FCSTD DOCUMENT  (FreeCAD 0.18.1R)
Label: LED_hole_test
License: All rights reserved
LicenseURL: http://en.wikipedia.org/wiki/All_rights_reserved
objects: Sketcher::SketchObject×1, PartDesign::Body×1
note: 2 computed .brp shape members not serialized (recipe doc carries the construction recipe); baked Part::Feature solids carry a one-line shape summary decoded from their .brp

FEATURE [Sketcher::SketchObject] Sketch
  MapMode = 5
  Support = -> [XY_Plane]
  sketch-geometry (28):
    g0: LineSegment StartX=0 StartY=0 StartZ=0 EndX=25 EndY=0 EndZ=0
    g1: LineSegment StartX=25 StartY=0 StartZ=0 EndX=25 EndY=30 EndZ=0
    g2: LineSegment StartX=25 StartY=30 StartZ=0 EndX=0 EndY=30 EndZ=0
    g3: LineSegment StartX=0 StartY=30 StartZ=0 EndX=0 EndY=0 EndZ=0
    g4: LineSegment StartX=4 StartY=4 StartZ=0 EndX=7.2 EndY=4 EndZ=0
    g5: LineSegment StartX=7.2 StartY=4 StartZ=0 EndX=7.2 EndY=7.2 EndZ=0
    g6: LineSegment StartX=7.2 StartY=7.2 StartZ=0 EndX=4 EndY=7.2 EndZ=0
    g7: LineSegment StartX=4 StartY=7.2 StartZ=0 EndX=4 EndY=4 EndZ=0
    g8: LineSegment StartX=11.2 StartY=4 StartZ=0 EndX=14.5 EndY=4 EndZ=0
    g9: LineSegment StartX=14.5 StartY=4 StartZ=0 EndX=14.5 EndY=7.3 EndZ=0
    g10: LineSegment StartX=14.5 StartY=7.3 StartZ=0 EndX=11.2 EndY=7.3 EndZ=0
    g11: LineSegment StartX=11.2 StartY=7.3 StartZ=0 EndX=11.2 EndY=4 EndZ=0
    g12: LineSegment StartX=18.5 StartY=4 StartZ=0 EndX=21.9 EndY=4 EndZ=0
    g13: LineSegment StartX=21.9 StartY=4 StartZ=0 EndX=21.9 EndY=7.4 EndZ=0
    g14: LineSegment StartX=21.9 StartY=7.4 StartZ=0 EndX=18.5 EndY=7.4 EndZ=0
    g15: LineSegment StartX=18.5 StartY=7.4 StartZ=0 EndX=18.5 EndY=4 EndZ=0
    g16: LineSegment StartX=4 StartY=10 StartZ=0 EndX=7.1 EndY=10 EndZ=0
    g17: LineSegment StartX=7.1 StartY=10 StartZ=0 EndX=7.1 EndY=13.1 EndZ=0
    g18: LineSegment StartX=7.1 StartY=13.1 StartZ=0 EndX=4 EndY=13.1 EndZ=0
    g19: LineSegment StartX=4 StartY=13.1 StartZ=0 EndX=4 EndY=10 EndZ=0
    g20: LineSegment StartX=11.1 StartY=10 StartZ=0 EndX=14.1 EndY=10 EndZ=0
    g21: LineSegment StartX=14.1 StartY=10 StartZ=0 EndX=14.1 EndY=13 EndZ=0
    g22: LineSegment StartX=14.1 StartY=13 StartZ=0 EndX=11.1 EndY=13 EndZ=0
    g23: LineSegment StartX=11.1 StartY=13 StartZ=0 EndX=11.1 EndY=10 EndZ=0
    g24: LineSegment StartX=18.1 StartY=10 StartZ=0 EndX=21.6 EndY=10 EndZ=0
    g25: LineSegment StartX=21.6 StartY=10 StartZ=0 EndX=21.6 EndY=13.5 EndZ=0
    g26: LineSegment StartX=21.6 StartY=13.5 StartZ=0 EndX=18.1 EndY=13.5 EndZ=0
    g27: LineSegment StartX=18.1 StartY=13.5 StartZ=0 EndX=18.1 EndY=10 EndZ=0
  constraints (83):
    c: Coincident(g0,g1)
    c: Coincident(g1,g2)
    c: Coincident(g2,g3)
    c: Coincident(g3,g0)
    c: Horizontal(g0)
    c: Horizontal(g2)
    c: Vertical(g1)
    c: Vertical(g3)
    c: Coincident(g0,g-1)
    c: DistanceX(g0,g0) = 25
    c: DistanceY(g3,g3) = 30
    c: Coincident(g4,g5)
    c: Coincident(g5,g6)
    c: Coincident(g6,g7)
    c: Coincident(g7,g4)
    c: Horizontal(g4)
    c: Horizontal(g6)
    c: Vertical(g5)
    c: Vertical(g7)
    c: DistanceY(g5,g5) = 3.2
    c: DistanceX(g6,g6) = 3.2
    c: DistanceY(g0,g4) = 4
    c: DistanceX(g0,g4) = 4
    c: Coincident(g8,g9)
    c: Coincident(g9,g10)
    c: Coincident(g10,g11)
    c: Coincident(g11,g8)
    c: Horizontal(g8)
    c: Horizontal(g10)
    c: Vertical(g9)
    c: Vertical(g11)
    c: DistanceX(g5,g10) = 4
    c: DistanceX(g10,g10) = 3.3
    c: DistanceY(g9,g9) = 3.3
    c: DistanceY(g0,g8) = 4
    c: Coincident(g12,g13)
    c: Coincident(g13,g14)
    c: Coincident(g14,g15)
    c: Coincident(g15,g12)
    c: Horizontal(g12)
    c: Horizontal(g14)
    c: Vertical(g13)
    c: Vertical(g15)
    c: DistanceX(g14,g14) = 3.4
    c: DistanceY(g13,g13) = 3.4
    c: DistanceY(g0,g12) = 4
    c: DistanceX(g9,g14) = 4
    c: Coincident(g16,g17)
    c: Coincident(g17,g18)
    c: Coincident(g18,g19)
    c: Coincident(g19,g16)
    c: Horizontal(g16)
    c: Horizontal(g18)
    c: Vertical(g17)
    c: Vertical(g19)
    c: Coincident(g20,g21)
    c: Coincident(g21,g22)
    c: Coincident(g22,g23)
    c: Coincident(g23,g20)
    c: Horizontal(g20)
    c: Horizontal(g22)
    c: Vertical(g21)
    c: Vertical(g23)
    c: Coincident(g24,g25)
    c: Coincident(g25,g26)
    c: Coincident(g26,g27)
    c: Coincident(g27,g24)
    c: Horizontal(g24)
    c: Horizontal(g26)
    c: Vertical(g25)
    c: Vertical(g27)
    c: DistanceX(g0,g16) = 4
    c: DistanceX(g17,g22) = 4
    c: DistanceX(g21,g26) = 4
    c: DistanceY(g0,g16) = 10
    c: DistanceY(g0,g20) = 10
    c: DistanceY(g0,g24) = 10
    c: DistanceY(g17,g17) = 3.1
    c: DistanceX(g18,g18) = 3.1
    c: DistanceX(g22,g22) = 3
    c: DistanceX(g26,g26) = 3.5
    c: DistanceY(g21,g21) = 3
    c: DistanceY(g25,g25) = 3.5
FEATURE [PartDesign::Body] Body
  Group = -> [Sketch]
  Origin = -> Origin
